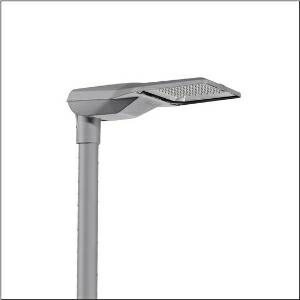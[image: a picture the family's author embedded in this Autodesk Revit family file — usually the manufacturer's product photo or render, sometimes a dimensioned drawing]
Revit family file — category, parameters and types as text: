
# Revit family: streetlight_sl_21_iq_midi___st1_0ab_5xe3m31g08nb_68e1
name_source: partatom
category: Lighting Fixtures
units: mm (PartAtom-declared; Revit-internal decimal feet)

## family parameters
Cut with Voids When Loaded = No
Host = Face
Light Source = No
Part Type = Normal
Room Calculation Point = No
Round Connector Dimension = Use Diameter
Shared = No

## types (1)
- --- (1 x LED, 20440 lm, 155.5 W, 3000K)
    Apparent Load = 155 VA
    CIE Flux Codes = 40 74 97 100 100
    Color Rendering = 70
    Color Temperature = 3000K
    Default Elevation = 1800 mm
    Description = Streetlight SL 21 iQ midi, mast luminaire, primary light control with lens, of PMMA, primary optical cover: cover, of toughened safety glass, transparent, light distribution: ST1.0aB, light emission: direct distribution, primary light characteristic: asymmetric, installation type: post-top, side-entry, LED, High Power LED, rated luminous flux: 20.440lm, luminous efficacy: 131lm/W, light colour: 730, colour temperature: 3000K, control gear: iQ Street-Remote, control: Street-Remote, Auto-Match, Temp-Guard, Lumen-Switch, Night-Set, Smart-Wire, Light-Fading, Desk-Remote (wireless, voltage-free reading and setting of iQ features in the workshop via application-optimized NFC function/RFID function), optimised constant luminous flux control (CLO 2.0), pre-setting: linear dimming characteristic, mains connection: 230..240V, AC, 50/60Hz, start of lifetime: 156W, end of service life: 162W, reduction: 69W, luminaire housing, of diecast aluminium, powder-coated, SITECO metallic grey (DB 702S), corrosivity category C5 high according to DIN EN ISO 12944, please order mast flange separately, inclination adjustable: 0°, 5°, 10°, 15°, sealing non-destructively replaceable, multi-level sealing system, length: 644mm, width: 335mm, height: 110mm, mast flange for spigot size: 42mm (side-entry): 5XC10008XM4, 60/48mm (side-entry/post-top): 5XC10108XM2, 76/60mm (side-entry/post-top): 5XC10108XM1, mounting height: 4..8m, protection rating (complete): IP66, insulation class (complete): insulation class II (safety insulation), certification: CE, ENEC, ENEC+, VDE, impact resistance: IK10, permissible operating ambient temperature for outdoor applications: -40..+50°C, standard-compliant lighting for roads and squares, packaging unit: 1 piece

Light Distribution: ST1.0aB
    Height = 111 mm
    Lamp = 1 x LED
    Lamp Light Flux = 20440 lm
    Lamp Power = 155.5 W
    Lamp count = 1
    Length = 644 mm
    Luminous efficacy = 131 lm/W
    Manufacturer = Siteco
    ModVariant = No
    Model = 5XE3M31G08NB
    Number of Poles = 1
    OnlyDefault = Yes
    Power Factor = 1
    Product Name = Streetlight SL 21 iQ midi | ST1.0aB
    Product group = mast luminaire | pylon top
    ProductGroupID = 6100
    Protection Class = Protection class II
    Protection Degree = IP 66
    RLX_Detail_Level = 1
    RLX_Emergency_Light_Flux = 0 lm
    RLX_Emergency_Type = 0
    RLX_Emergency_Type_DB = No
    RlxData = <blob elided: 27133 chars, md5=c13ee05f>
    Socket = socket
    Standby Power = 0 W
    System Light Flux = 20440 lm
    System Power = 155 W
    Type Comments = factory setting: luminous flux: 100 % | dim-lin: 254 | 823 mA
    Type Image = l_1004298.jpg
    URL = http://relux.com
    VarID = @adj_167699
    Voltage = 0 V
    Weight = 0.00 kg
    Width = 336 mm

## geometry (parser evidence)
native form markers: Blend x4, Sweep x13
no freeform markers — native parametric forms only
